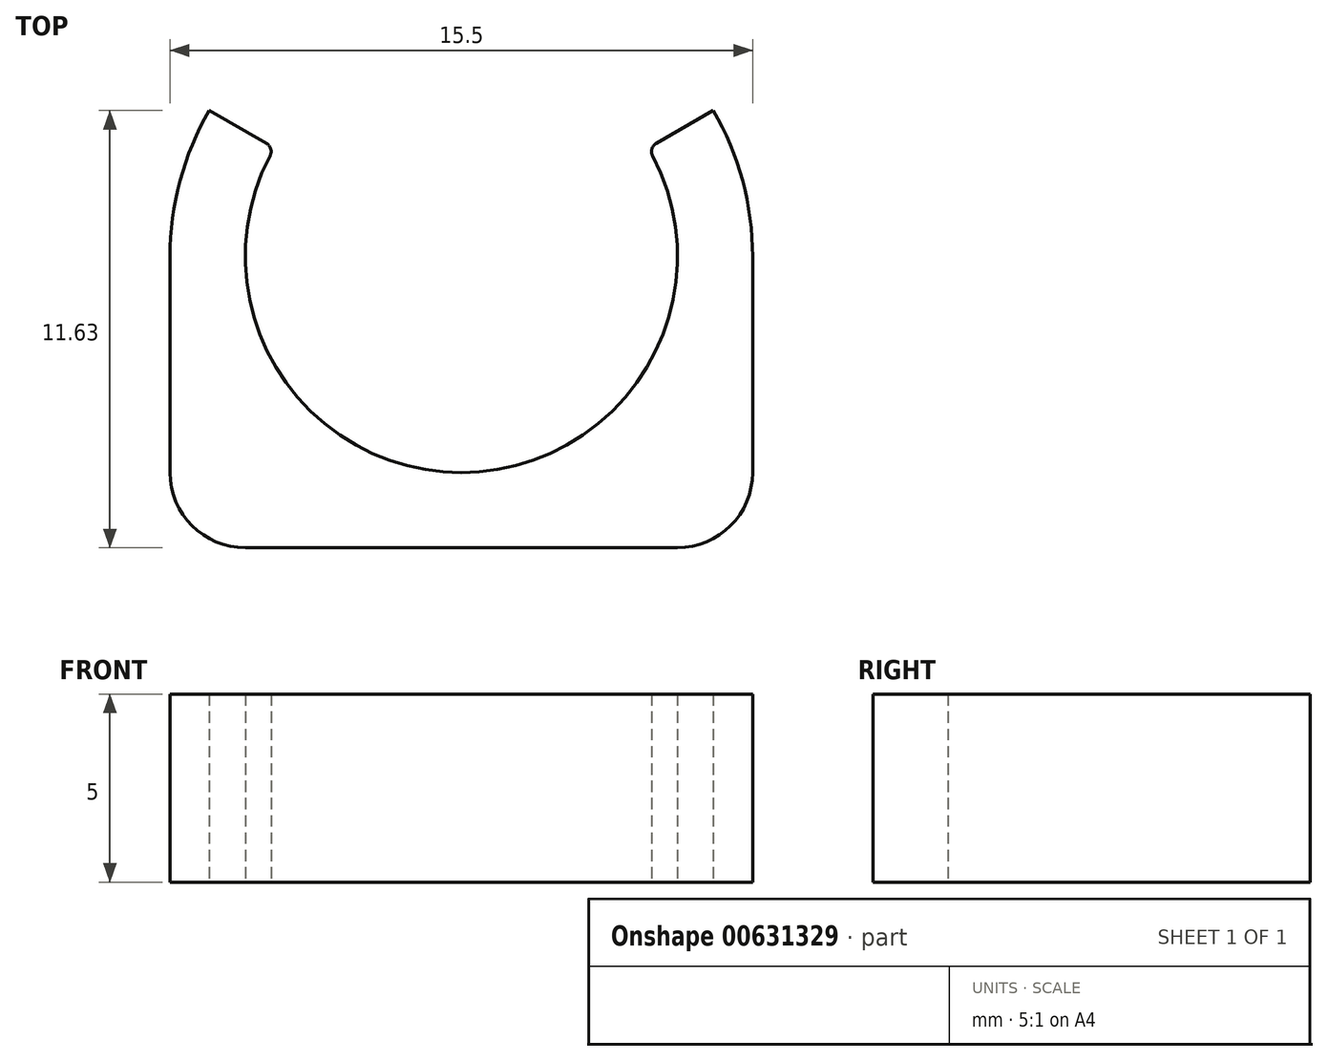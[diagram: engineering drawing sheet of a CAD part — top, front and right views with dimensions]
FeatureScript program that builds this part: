
annotation { "Feature Type Name" : "Feature", "Feature Type Description" : "" }
export const myFeature = defineFeature(function(context is Context, id is Id, definition is map)
    precondition{}
    {
        {
            var Q0;
            Q0=qCreatedBy(makeId("Top.planeOp"),FACE);
            var sketch = newSketch(context, id + "F0", { "sketchPlane" : qUnion([Q0])});
            skArc(sketch, "E0", {"start": v(-5.1, 2.67) * mm, "mid": v(0, -5.75) * mm, "end": v(5.1, 2.67) * mm});
            skArc(sketch, "E1.0", {"start": v(-6.7, 3.88) * mm, "mid": v(0, -7.75) * mm, "end": v(6.7, 3.88) * mm});
            skLineSegment(sketch, "E2", {"start": v(-5.19, 3) * mm, "end": v(-6.7, 3.88) * mm});
            skLineSegment(sketch, "E3", {"start": v(5.19, 3) * mm, "end": v(6.7, 3.88) * mm});
            skLineSegment(sketch, "E4", {"start": v(0, -7.75) * mm, "end": v(-7.75, -7.75) * mm});
            skLineSegment(sketch, "E5", {"start": v(-5.75, -7.75) * mm, "end": v(5.75, -7.75) * mm});
            skLineSegment(sketch, "E6", {"start": v(7.75, 0) * mm, "end": v(7.75, -5.75) * mm});
            skLineSegment(sketch, "E7", {"start": v(-7.75, 0) * mm, "end": v(-7.75, -5.75) * mm});
            skPoint(sketch, "E8.visualSharp", {"position": v(-4.97, 2.88) * mm});
            skArc(sketch, "E8.filletArc", {"start": v(-5.1, 2.67) * mm, "mid": v(-5.07, 2.86) * mm, "end": v(-5.19, 3) * mm});
            skPoint(sketch, "E9.visualSharp", {"position": v(4.97, 2.88) * mm});
            skArc(sketch, "E9.filletArc", {"start": v(5.19, 3) * mm, "mid": v(5.07, 2.86) * mm, "end": v(5.1, 2.67) * mm});
            skPoint(sketch, "E10.visualSharp", {"position": v(-7.75, -7.75) * mm});
            skArc(sketch, "E10.filletArc", {"start": v(-7.75, -5.75) * mm, "mid": v(-7.16, -7.16) * mm, "end": v(-5.75, -7.75) * mm});
            skPoint(sketch, "E11.visualSharp", {"position": v(7.75, -7.75) * mm});
            skArc(sketch, "E11.filletArc", {"start": v(5.75, -7.75) * mm, "mid": v(7.16, -7.16) * mm, "end": v(7.75, -5.75) * mm});
            skSolve(sketch);
        }
        {
            var Q0;
            Q0=makeQuery(id+"F0.imprint","IMPRINT",FACE,{"disambiguationData":[TD([[makeQuery(id+"F0.imprint","IMPRINT",EDGE,{"derivedFrom":sQuery(id+"F0.wireOp",EDGE,"E0")}),-1.0]])]});
            var Q1;
            {var subQ0=sQuery(id+"F0.wireOp",EDGE,"E7");Q1=makeQuery(id+"F0.imprint","IMPRINT",FACE,{"disambiguationData":[TD([[makeQuery(id+"F0.imprint","IMPRINT",EDGE,{"derivedFrom":subQ0}),1.0]])]});}
            var Q2;
            {var subQ0=sQuery(id+"F0.wireOp",EDGE,"E6");Q2=makeQuery(id+"F0.imprint","IMPRINT",FACE,{"disambiguationData":[TD([[makeQuery(id+"F0.imprint","IMPRINT",EDGE,{"derivedFrom":subQ0}),-1.0]])]});}
            extrude(context, id + "F1", {"entities" : qUnion([Q0, Q1, Q2]), "depth" : 5 * mm, "offsetDistance" : 25 * mm});
        }
    });
